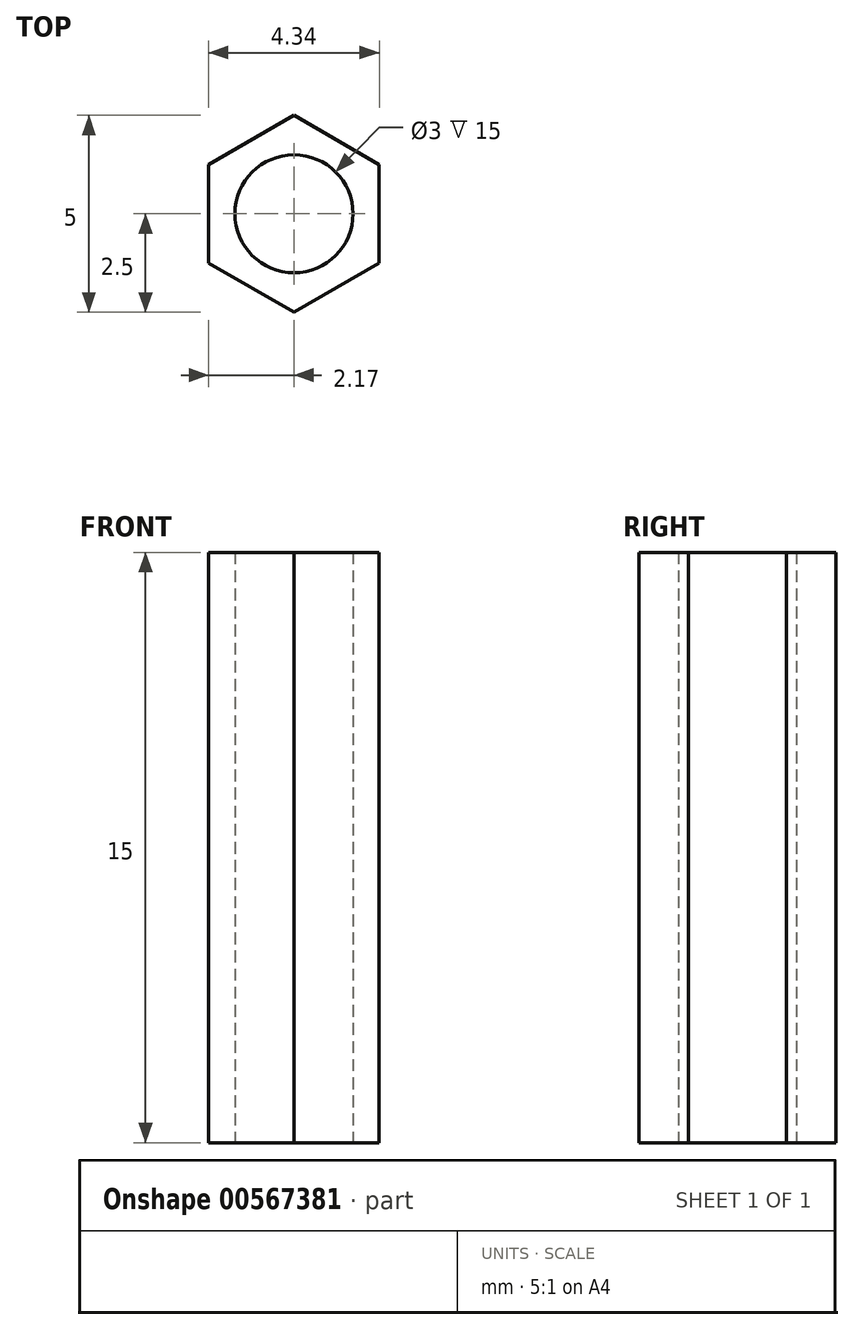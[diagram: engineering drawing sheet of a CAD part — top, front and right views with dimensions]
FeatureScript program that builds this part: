
annotation { "Feature Type Name" : "Feature", "Feature Type Description" : "" }
export const myFeature = defineFeature(function(context is Context, id is Id, definition is map)
    precondition{}
    {
        {
            var Q0;
            Q0=qCreatedBy(makeId("Top.planeOp"),FACE);
            var sketch = newSketch(context, id + "F0", { "sketchPlane" : qUnion([Q0])});
            skCircle(sketch, "E0.cCircle", {"center": v(0, 0) * mm, "radius": 2.5 * mm, "construction": true});
            skLineSegment(sketch, "E0.0", {"start": v(-2.17, -1.25) * mm, "end": v(-2.17, 1.25) * mm});
            skLineSegment(sketch, "E0.1", {"start": v(-2.17, 1.25) * mm, "end": v(0, 2.5) * mm});
            skLineSegment(sketch, "E0.2", {"start": v(0, 2.5) * mm, "end": v(2.17, 1.25) * mm});
            skLineSegment(sketch, "E0.3", {"start": v(2.17, 1.25) * mm, "end": v(2.17, -1.25) * mm});
            skLineSegment(sketch, "E0.4", {"start": v(2.17, -1.25) * mm, "end": v(0, -2.5) * mm});
            skLineSegment(sketch, "E0.5", {"start": v(0, -2.5) * mm, "end": v(-2.17, -1.25) * mm});
            skCircle(sketch, "E1", {"center": v(0, 0) * mm, "radius": 1.5 * mm});
            skSolve(sketch);
        }
        {
            var Q0;
            Q0=qSketchRegion(id+"F0",true);
            extrude(context, id + "F1", {"entities" : qUnion([Q0]), "depth" : 15 * mm, "offsetDistance" : 25 * mm});
        }
    });
